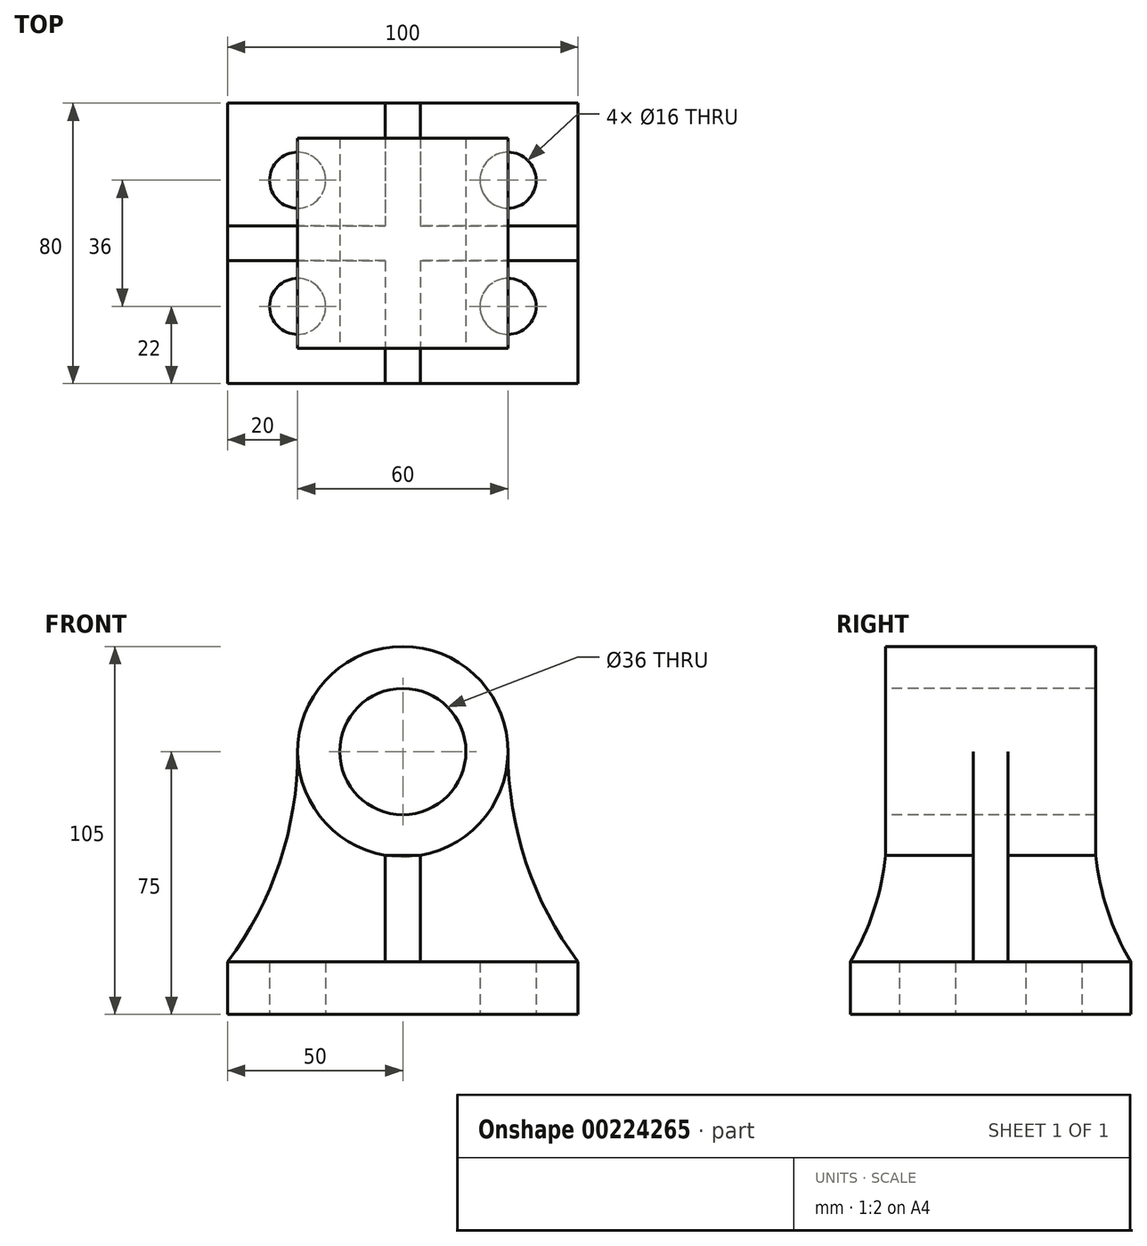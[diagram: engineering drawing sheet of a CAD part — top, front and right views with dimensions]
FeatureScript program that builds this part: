
annotation { "Feature Type Name" : "Feature", "Feature Type Description" : "" }
export const myFeature = defineFeature(function(context is Context, id is Id, definition is map)
    precondition{}
    {
        {
            var Q0;
            Q0=qCreatedBy(makeId("Front.planeOp"),FACE);
            var sketch = newSketch(context, id + "F0", { "sketchPlane" : qUnion([Q0])});
            skCircle(sketch, "E0", {"center": v(0, 0) * mm, "radius": 30 * mm});
            skCircle(sketch, "E1", {"center": v(0, 0) * mm, "radius": 18 * mm});
            skLineSegment(sketch, "E2.bottom", {"start": v(50, -60) * mm, "end": v(-50, -60) * mm});
            skLineSegment(sketch, "E2.top", {"start": v(50, -75) * mm, "end": v(-50, -75) * mm});
            skLineSegment(sketch, "E2.left", {"start": v(50, -60) * mm, "end": v(50, -75) * mm});
            skLineSegment(sketch, "E2.right", {"start": v(-50, -60) * mm, "end": v(-50, -75) * mm});
            skPoint(sketch, "E2.middle", {"position": v(0, -67.5) * mm});
            skLineSegment(sketch, "E3", {"start": v(-5, -29.58) * mm, "end": v(-5, -60) * mm});
            skLineSegment(sketch, "E4", {"start": v(5, -29.58) * mm, "end": v(5, -60) * mm});
            skArc(sketch, "E5", {"start": v(-50, -60) * mm, "mid": v(-35.13, -31.62) * mm, "end": v(-30, 0) * mm});
            skArc(sketch, "E6.MirrorCS", {"start": v(50, -60) * mm, "mid": v(35.13, -31.62) * mm, "end": v(30, 0) * mm});
            skSolve(sketch);
        }
        {
            var Q0;
            Q0=makeQuery(id+"F0.imprint","IMPRINT",FACE,{"disambiguationData":[TD([[makeQuery(id+"F0.imprint","IMPRINT",EDGE,{"derivedFrom":sQuery(id+"F0.wireOp",EDGE,"E2.top")}),-1.0]])]});
            var Q1;
            {var subQ0=sQuery(id+"F0.wireOp",EDGE,"E3");Q1=makeQuery(id+"F0.imprint","IMPRINT",FACE,{"disambiguationData":[TD([[makeQuery(id+"F0.imprint","IMPRINT",EDGE,{"derivedFrom":subQ0}),1.0]])]});}
            extrude(context, id + "F1", {"entities" : qUnion([Q0, Q1]), "endBound" : BoundingType.SYMMETRIC, "oppositeDirection" : true, "depth" : 80 * mm});
        }
        {
            var Q0;
            Q0=makeQuery(id+"F0.imprint","IMPRINT",FACE,{"disambiguationData":[TD([[makeQuery(id+"F0.imprint","IMPRINT",EDGE,{"derivedFrom":sQuery(id+"F0.wireOp",EDGE,"E1")}),-1.0]])]});
            extrude(context, id + "F2", {"entities" : qUnion([Q0]), "operationType" : NewBodyOperationType.ADD, "endBound" : BoundingType.SYMMETRIC, "oppositeDirection" : true, "depth" : 60 * mm});
        }
        {
            var Q0;
            Q0=qCreatedBy(makeId("Right.planeOp"),FACE);
            var sketch = newSketch(context, id + "F3", { "sketchPlane" : qUnion([Q0])});
            skArc(sketch, "E7", {"start": v(-40, -60) * mm, "mid": v(-33.33, -45.33) * mm, "end": v(-29.96, -29.58) * mm});
            skLineSegment(sketch, "E8.0", {"start": v(-30, -29.58) * mm, "end": v(-40, -29.58) * mm});
            skLineSegment(sketch, "E9.0", {"start": v(-40, -29.58) * mm, "end": v(-40, -60) * mm});
            skLineSegment(sketch, "E10.0.0", {"start": v(-40, -60) * mm, "end": v(-40, -29.58) * mm});
            skLineSegment(sketch, "E10.0.1", {"start": v(-40, -29.58) * mm, "end": v(-30, -29.58) * mm});
            skLineSegment(sketch, "E10.0.2", {"start": v(-30, -29.58) * mm, "end": v(30, -29.58) * mm});
            skLineSegment(sketch, "E10.0.3", {"start": v(30, -29.58) * mm, "end": v(40, -29.58) * mm});
            skLineSegment(sketch, "E10.0.4", {"start": v(40, -29.58) * mm, "end": v(40, -60) * mm});
            skLineSegment(sketch, "E10.0.5", {"start": v(40, -60) * mm, "end": v(-40, -60) * mm});
            skSolve(sketch);
        }
        {
            var Q0;
            {var subQ0=sQuery(id+"F3.wireOp",EDGE,"E7");Q0=makeQuery(id+"F3.imprint","IMPRINT",FACE,{"disambiguationData":[TD([[makeQuery(id+"F3.imprint","IMPRINT",EDGE,{"derivedFrom":subQ0}),1.0]])]});}
            extrude(context, id + "F4", {"entities" : qUnion([Q0]), "operationType" : NewBodyOperationType.REMOVE, "endBound" : BoundingType.SYMMETRIC, "oppositeDirection" : true, "depth" : 25 * mm});
        }
        {
            var Q0;
            Q0=qCreatedBy(makeId("Right.planeOp"),FACE);
            var sketch = newSketch(context, id + "F5", { "sketchPlane" : qUnion([Q0])});
            skArc(sketch, "E11", {"start": v(30, -29.58) * mm, "mid": v(33.36, -45.33) * mm, "end": v(40, -60) * mm});
            skLineSegment(sketch, "E12.0", {"start": v(-30, -29.58) * mm, "end": v(30, -29.58) * mm});
            skLineSegment(sketch, "E13.0", {"start": v(30, -29.58) * mm, "end": v(40, -29.58) * mm});
            skLineSegment(sketch, "E14.0", {"start": v(40, -29.58) * mm, "end": v(40, -60) * mm});
            skLineSegment(sketch, "E15.0", {"start": v(40, -60) * mm, "end": v(-40, -60) * mm});
            skSolve(sketch);
        }
        {
            var Q0;
            Q0=makeQuery(id+"F5.imprint","IMPRINT",FACE,{"disambiguationData":[TD([[makeQuery(id+"F5.imprint","IMPRINT",EDGE,{"derivedFrom":sQuery(id+"F5.wireOp",EDGE,"E11")}),1.0]])]});
            extrude(context, id + "F6", {"entities" : qUnion([Q0]), "operationType" : NewBodyOperationType.REMOVE, "endBound" : BoundingType.SYMMETRIC, "oppositeDirection" : true, "depth" : 25 * mm});
        }
        {
            var Q0;
            {var subQ0=sQuery(id+"F0.wireOp",EDGE,"E4");Q0=makeQuery(id+"F0.imprint","IMPRINT",FACE,{"disambiguationData":[TD([[makeQuery(id+"F0.imprint","IMPRINT",EDGE,{"derivedFrom":subQ0}),1.0]])]});}
            var Q1;
            {var subQ0=sQuery(id+"F0.wireOp",EDGE,"E3");Q1=makeQuery(id+"F0.imprint","IMPRINT",FACE,{"disambiguationData":[TD([[makeQuery(id+"F0.imprint","IMPRINT",EDGE,{"derivedFrom":subQ0}),-1.0]])]});}
            extrude(context, id + "F7", {"entities" : qUnion([Q0, Q1]), "operationType" : NewBodyOperationType.ADD, "endBound" : BoundingType.SYMMETRIC, "depth" : 10 * mm});
        }
        {
            var Q0;
            Q0=makeQuery(id+"F1.opExtrude","SWEPT_FACE",FACE,{"disambiguationData":[OSD([sQuery(id+"F0.wireOp",EDGE,"E2.top")])]});
            var sketch = newSketch(context, id + "F8", { "sketchPlane" : qUnion([Q0])});
            skCircle(sketch, "E16", {"center": v(-30, 18) * mm, "radius": 8 * mm});
            skCircle(sketch, "E17", {"center": v(-30, -18) * mm, "radius": 8 * mm});
            skCircle(sketch, "E18", {"center": v(30, -18) * mm, "radius": 8 * mm});
            skCircle(sketch, "E19", {"center": v(30, 18) * mm, "radius": 8 * mm});
            skSolve(sketch);
        }
        {
            var Q0;
            Q0=makeQuery(id+"F8.imprint","IMPRINT",FACE,{"disambiguationData":[TD([[makeQuery(id+"F8.imprint","IMPRINT",EDGE,{"derivedFrom":sQuery(id+"F8.wireOp",EDGE,"E18")}),1.0]])]});
            var Q1;
            Q1=makeQuery(id+"F8.imprint","IMPRINT",FACE,{"disambiguationData":[TD([[makeQuery(id+"F8.imprint","IMPRINT",EDGE,{"derivedFrom":sQuery(id+"F8.wireOp",EDGE,"E17")}),1.0]])]});
            var Q2;
            Q2=makeQuery(id+"F8.imprint","IMPRINT",FACE,{"disambiguationData":[TD([[makeQuery(id+"F8.imprint","IMPRINT",EDGE,{"derivedFrom":sQuery(id+"F8.wireOp",EDGE,"E16")}),1.0]])]});
            var Q3;
            Q3=makeQuery(id+"F8.imprint","IMPRINT",FACE,{"disambiguationData":[TD([[makeQuery(id+"F8.imprint","IMPRINT",EDGE,{"derivedFrom":sQuery(id+"F8.wireOp",EDGE,"E19")}),1.0]])]});
            extrude(context, id + "F9", {"entities" : qUnion([Q0, Q1, Q2, Q3]), "operationType" : NewBodyOperationType.REMOVE, "oppositeDirection" : true, "depth" : 15 * mm});
        }
    });
